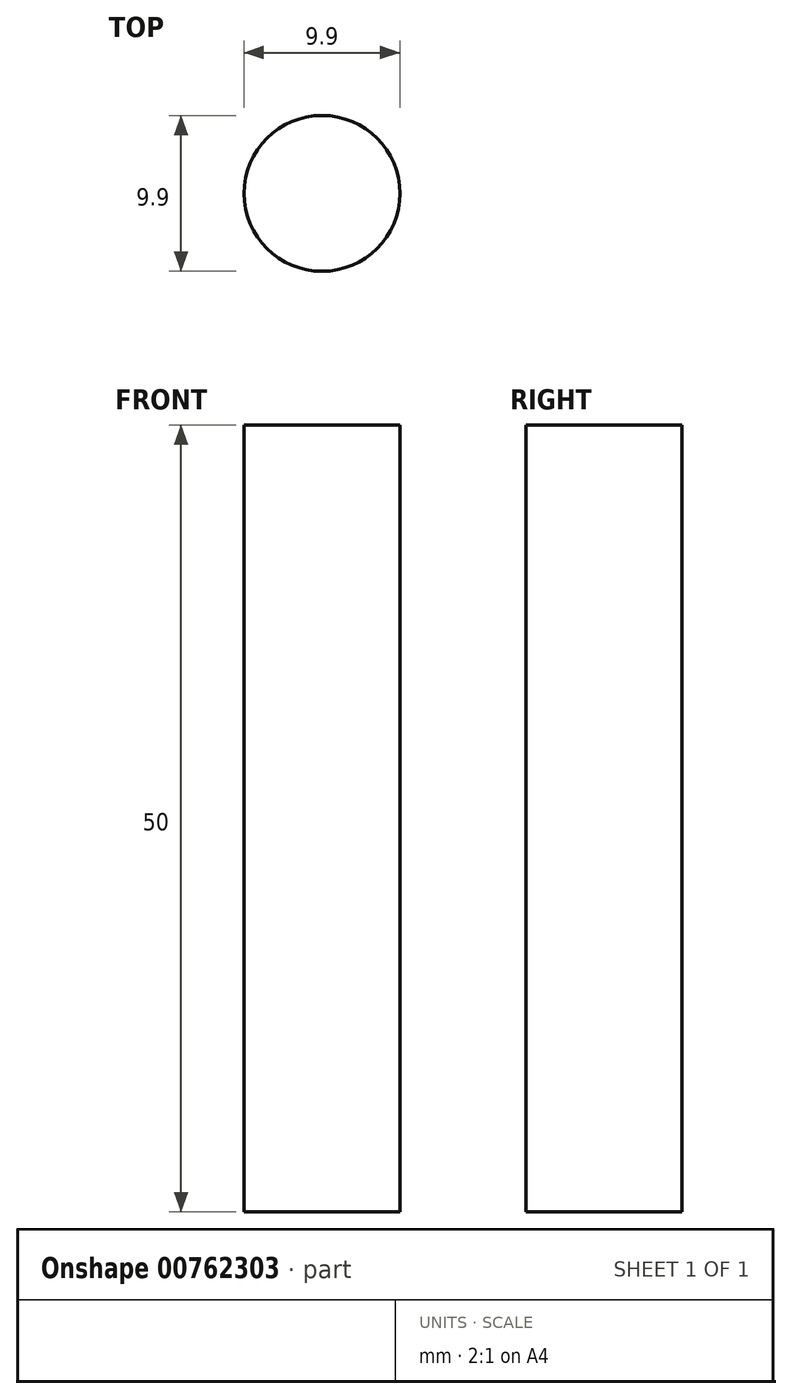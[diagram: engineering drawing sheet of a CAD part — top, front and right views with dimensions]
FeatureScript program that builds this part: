
annotation { "Feature Type Name" : "Feature", "Feature Type Description" : "" }
export const myFeature = defineFeature(function(context is Context, id is Id, definition is map)
    precondition{}
    {
        {
            var Q0;
            Q0=qCreatedBy(makeId("Top.planeOp"),FACE);
            var sketch = newSketch(context, id + "F0", { "sketchPlane" : qUnion([Q0])});
            skCircle(sketch, "E0", {"center": v(0, 0) * mm, "radius": 4.95 * mm});
            skSolve(sketch);
        }
        {
            var Q0;
            Q0 = qSketchRegion(id + "F0", true);
            extrude(context, id + "F1", {"entities" : qUnion([Q0]), "endBound" : BoundingType.SYMMETRIC, "depth" : 50 * mm, "offsetDistance" : 25 * mm});
        }
    });
